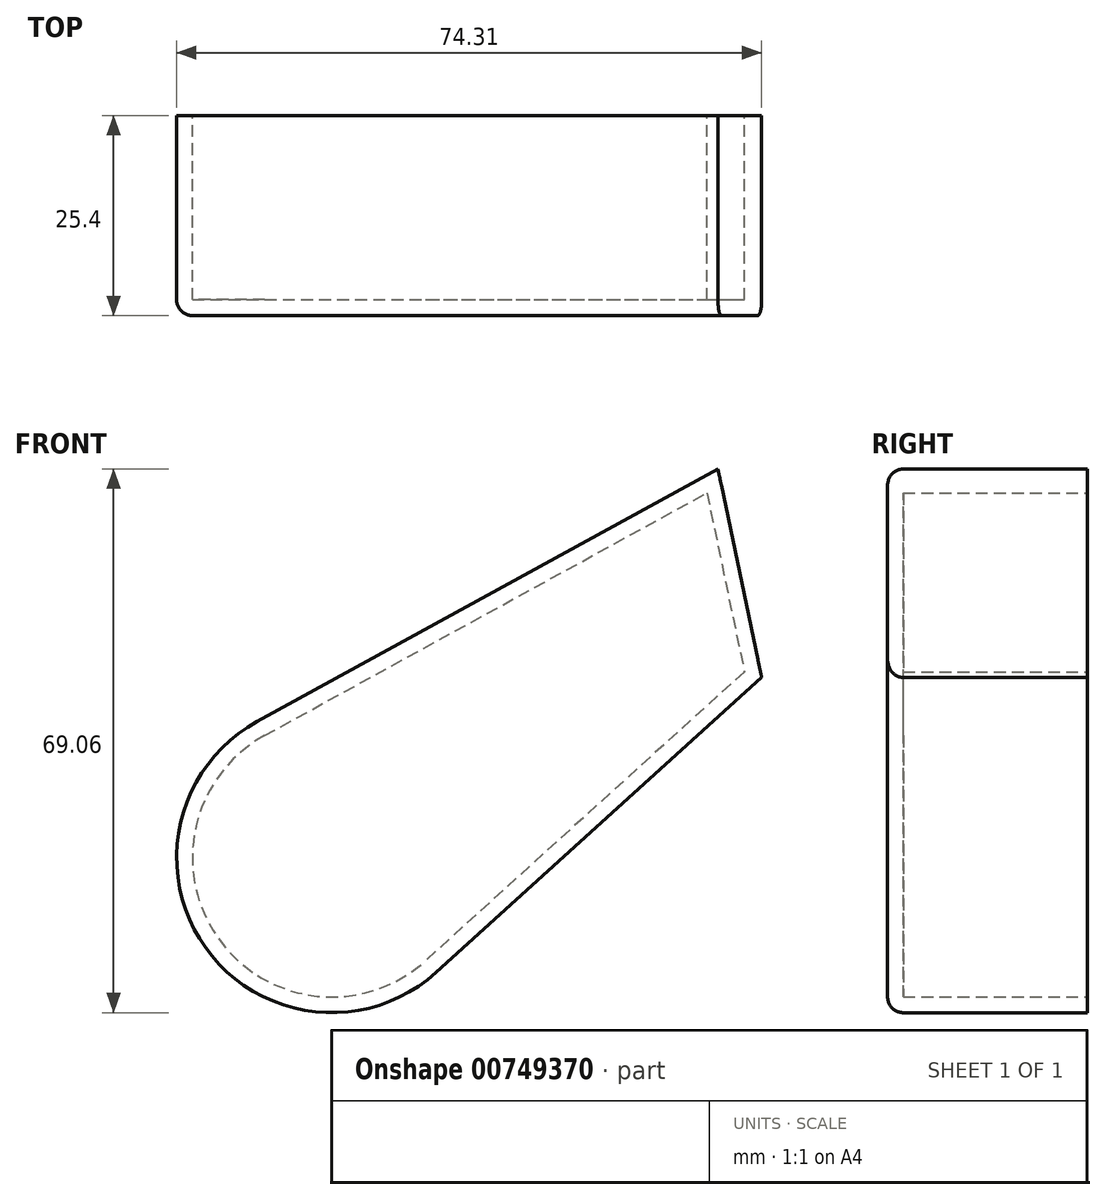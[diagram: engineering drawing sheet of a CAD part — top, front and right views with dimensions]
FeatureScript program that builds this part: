
annotation { "Feature Type Name" : "Feature", "Feature Type Description" : "" }
export const myFeature = defineFeature(function(context is Context, id is Id, definition is map)
    precondition{}
    {
        {
            var Q0;
            Q0=qCreatedBy(makeId("Front.planeOp"),FACE);
            var sketch = newSketch(context, id + "F0", { "sketchPlane" : qUnion([Q0])});
            skLineSegment(sketch, "E0", {"start": v(-110.03, 29.44) * mm, "end": v(-51.5, 61.53) * mm});
            skLineSegment(sketch, "E1", {"start": v(-51.5, 61.53) * mm, "end": v(-45.95, 35.06) * mm});
            skArc(sketch, "E2", {"start": v(-110.03, 29.44) * mm, "mid": v(-116.6, 0.74) * mm, "end": v(-87.33, -2.43) * mm});
            skLineSegment(sketch, "E3", {"start": v(-45.95, 35.06) * mm, "end": v(-87.33, -2.43) * mm});
            skSolve(sketch);
        }
        {
            var Q0;
            Q0 = qSketchRegion(id + "F0", true);
            extrude(context, id + "F1", {"entities" : qUnion([Q0]), "depth" : 25.4 * mm, "offsetDistance" : 25.4 * mm});
        }
        {
            var Q0;
            Q0=makeQuery(id+"F1.opExtrude","CAP_EDGE",EDGE,{"disambiguationData":[OSD([sQuery(id+"F0.wireOp",EDGE,"E0")])],"isStart":false});
            fillet(context, id + "F2", {"entities" : qUnion([Q0]), "radius" : 2 * mm, "tangentPropagation" : true, "allowEdgeOverflow" : false});
        }
        {
            var Q0;
            Q0=makeQuery(id+"F1.opExtrude","CAP_FACE",FACE,{"disambiguationData":[OSD([sQuery(id+"F0.wireOp",EDGE,"E0"),sQuery(id+"F0.wireOp",EDGE,"E1"),sQuery(id+"F0.wireOp",EDGE,"E2"),sQuery(id+"F0.wireOp",EDGE,"E3")])],"isStart":true});
            shell(context, id + "F3", {"entities" : qUnion([Q0]), "thickness" : 2 * mm});
        }
    });
